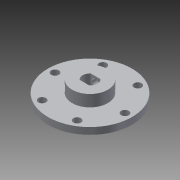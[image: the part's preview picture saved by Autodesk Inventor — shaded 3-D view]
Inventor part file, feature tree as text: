
AUTODESK INVENTOR PART (.ipt)
format: ipt  version: 2013 (Build 170138000, 138)  size: 128,512 bytes
history: native  units: in
note: dims shown in document units (in); Inventor stores cm internally (conversion verified against a paired STEP export)
features: extrude x3, sketch x3
ambient origin geometry x8: Origin, YZ Plane, XZ Plane, XY Plane, X Axis, Y Axis, Z Axis, Center Point
bodies: Solid1 (feature_tree)
feature tree (6):
  extrude  "Extrusion1"  Depth=1.875in
  extrude  "Extrusion2"  Depth=2.3622in TaperAngle=360.0deg
  extrude  "Extrusion3"  Depth=0.2955in
  sketch  "Sketch1"  dims[d0=2.25in d1=1.875in]
  sketch  "Sketch2"  dims[d2=0.204in d3=2.3622in d5=360.0deg]
  sketch  "Sketch3"  dims[d7=0.3935in d8=0.2955in d9=0.1478in d10=0.18in d11=0.0in d12=0.958in d14=0.31in d15=0.0in d16=0.19in d17=0.15in d18=0.1299in d19=0.31in d20=0.0in]
